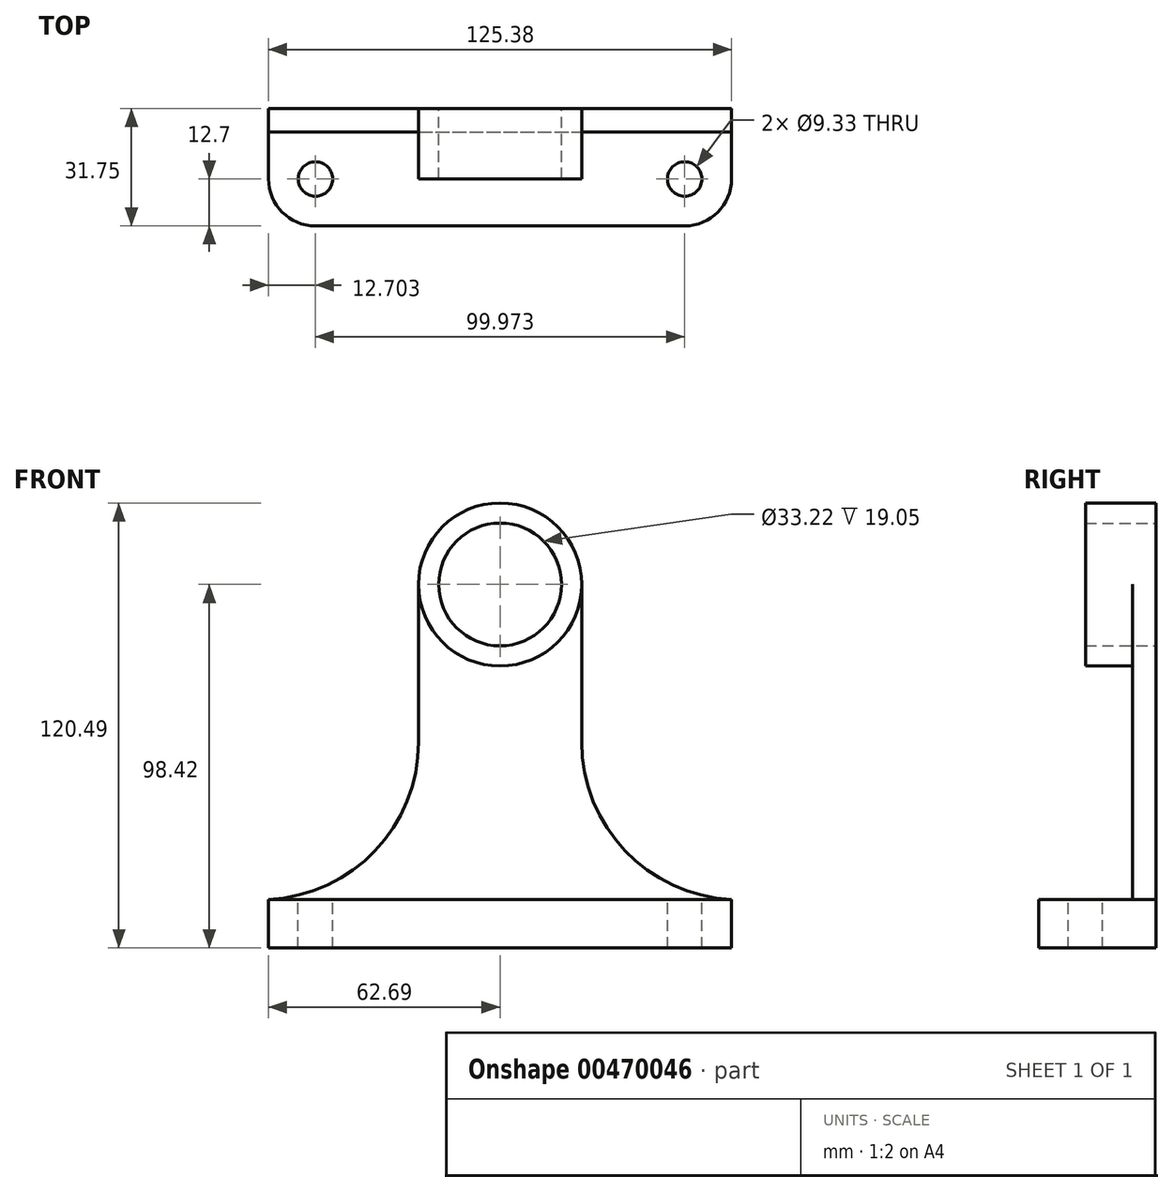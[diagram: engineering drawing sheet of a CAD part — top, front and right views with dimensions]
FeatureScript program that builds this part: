
annotation { "Feature Type Name" : "Feature", "Feature Type Description" : "" }
export const myFeature = defineFeature(function(context is Context, id is Id, definition is map)
    precondition{}
    {
        {
            var Q0;
            Q0=qCreatedBy(makeId("Front.planeOp"),FACE);
            var sketch = newSketch(context, id + "F0", { "sketchPlane" : qUnion([Q0])});
            skCircle(sketch, "E0", {"center": v(0, 0) * mm, "radius": 16.61 * mm});
            skCircle(sketch, "E1", {"center": v(0, 0) * mm, "radius": 22.07 * mm});
            skLineSegment(sketch, "E2.top", {"start": v(-22.07, -85.27) * mm, "end": v(22.07, -85.27) * mm});
            skLineSegment(sketch, "E2.left", {"start": v(-22.07, 0) * mm, "end": v(-22.07, -42.63) * mm});
            skLineSegment(sketch, "E2.right", {"start": v(22.07, 0) * mm, "end": v(22.07, -42.63) * mm});
            skLineSegment(sketch, "E3", {"start": v(22.07, -85.27) * mm, "end": v(62.69, -85.27) * mm});
            skLineSegment(sketch, "E4", {"start": v(62.69, -85.27) * mm, "end": v(62.69, -98.42) * mm});
            skLineSegment(sketch, "E5", {"start": v(62.69, -98.42) * mm, "end": v(-62.69, -98.42) * mm});
            skLineSegment(sketch, "E6", {"start": v(-62.69, -98.42) * mm, "end": v(-62.69, -85.27) * mm});
            skLineSegment(sketch, "E7", {"start": v(-62.69, -85.27) * mm, "end": v(-22.07, -85.27) * mm});
            skArc(sketch, "E8", {"start": v(22.07, -42.63) * mm, "mid": v(33.85, -72.07) * mm, "end": v(62.69, -85.27) * mm});
            skPoint(sketch, "E8.second.point", {"position": v(62.69, 0) * mm});
            skPoint(sketch, "E8.third.point", {"position": v(22.07, -42.63) * mm});
            skArc(sketch, "E9", {"start": v(-62.69, -85.27) * mm, "mid": v(-33.85, -72.07) * mm, "end": v(-22.07, -42.63) * mm});
            skPoint(sketch, "E9.second.point", {"position": v(-62.69, 0) * mm});
            skPoint(sketch, "E9.third.point", {"position": v(-22.07, -42.63) * mm});
            skSolve(sketch);
        }
        {
            var Q0;
            Q0=makeQuery(id+"F0.imprint","IMPRINT",FACE,{"disambiguationData":[TD([[makeQuery(id+"F0.imprint","IMPRINT",EDGE,{"derivedFrom":sQuery(id+"F0.wireOp",EDGE,"E2.top")}),1.0]])]});
            extrude(context, id + "F1", {"entities" : qUnion([Q0]), "depth" : 6.35 * mm});
        }
        {
            var Q0;
            Q0=makeQuery(id+"F0.imprint","IMPRINT",FACE,{"disambiguationData":[TD([[makeQuery(id+"F0.imprint","IMPRINT",EDGE,{"derivedFrom":sQuery(id+"F0.wireOp",EDGE,"E0")}),-1.0]])]});
            extrude(context, id + "F2", {"entities" : qUnion([Q0]), "operationType" : NewBodyOperationType.ADD, "depth" : 19.05 * mm});
        }
        {
            var Q0;
            Q0=makeQuery(id+"F0.imprint","IMPRINT",FACE,{"disambiguationData":[TD([[makeQuery(id+"F0.imprint","IMPRINT",EDGE,{"derivedFrom":sQuery(id+"F0.wireOp",EDGE,"E2.top")}),-1.0]])]});
            extrude(context, id + "F3", {"entities" : qUnion([Q0]), "operationType" : NewBodyOperationType.ADD, "depth" : 31.75 * mm});
        }
        {
            var Q0;
            Q0=makeQuery(id+"F3.opExtrude","SWEPT_FACE",FACE,{"disambiguationData":[OSD([sQuery(id+"F0.wireOp",EDGE,"E2.top"),sQuery(id+"F0.wireOp",EDGE,"E3"),sQuery(id+"F0.wireOp",EDGE,"E7")])]});
            var sketch = newSketch(context, id + "F4", { "sketchPlane" : qUnion([Q0])});
            skLineSegment(sketch, "E10", {"start": v(-62.69, -31.75) * mm, "end": v(-62.69, -19.05) * mm});
            skLineSegment(sketch, "E11", {"start": v(-62.69, -19.05) * mm, "end": v(-62.69, -19.05) * mm});
            skLineSegment(sketch, "E12", {"start": v(49.99, -31.75) * mm, "end": v(-49.99, -31.75) * mm});
            skLineSegment(sketch, "E13", {"start": v(62.69, -19.05) * mm, "end": v(62.69, -19.05) * mm});
            skPoint(sketch, "E14.visualSharp", {"position": v(-62.69, -31.75) * mm});
            skArc(sketch, "E14.filletArc", {"start": v(-62.69, -19.05) * mm, "mid": v(-58.97, -28.03) * mm, "end": v(-49.99, -31.75) * mm});
            skPoint(sketch, "E15.visualSharp", {"position": v(62.69, -31.75) * mm});
            skArc(sketch, "E15.filletArc", {"start": v(49.99, -31.75) * mm, "mid": v(58.97, -28.03) * mm, "end": v(62.69, -19.05) * mm});
            skCircle(sketch, "E16", {"center": v(-49.99, -19.05) * mm, "radius": 4.66 * mm});
            skCircle(sketch, "E17", {"center": v(49.99, -19.05) * mm, "radius": 4.66 * mm});
            skSolve(sketch);
        }
        {
            var Q0;
            Q0 = qSketchRegion(id + "F4", true);
            var Q1;
            {var subQ0=sQuery(id+"F4.wireOp",EDGE,"E10");Q1=makeQuery(id+"F4.imprint","IMPRINT",FACE,{"disambiguationData":[TD([[makeQuery(id+"F4.imprint","IMPRINT",EDGE,{"derivedFrom":subQ0}),-1.0]])]});}
            var Q2;
            {var subQ0=sQuery(id+"F4.wireOp",EDGE,"E15.filletArc");Q2=makeQuery(id+"F4.imprint","IMPRINT",FACE,{"disambiguationData":[TD([[makeQuery(id+"F4.imprint","IMPRINT",EDGE,{"derivedFrom":subQ0}),-1.0]])]});}
            extrude(context, id + "F5", {"entities" : qUnion([Q0, Q1, Q2]), "operationType" : NewBodyOperationType.REMOVE, "endBound" : BoundingType.THROUGH_ALL, "oppositeDirection" : true, "depth" : 25.4 * mm});
        }
    });
